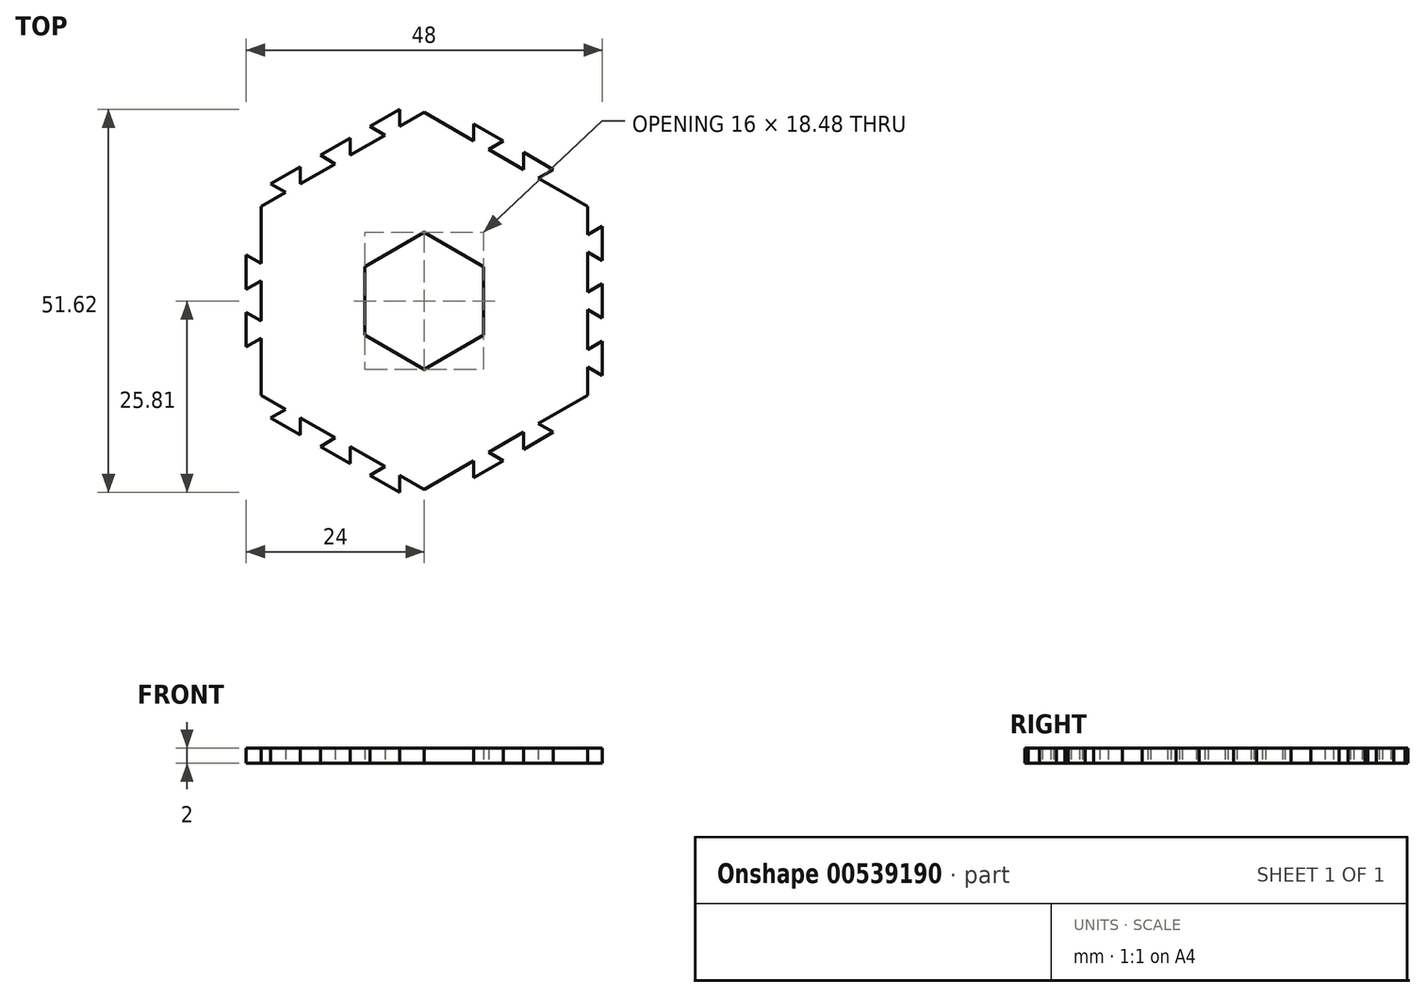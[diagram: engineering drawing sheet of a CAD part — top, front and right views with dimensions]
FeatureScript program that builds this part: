
annotation { "Feature Type Name" : "Feature", "Feature Type Description" : "" }
export const myFeature = defineFeature(function(context is Context, id is Id, definition is map)
    precondition{}
    {
        {
            assignVariable(context, id + "F0", {"name" : "thick", "anyValue" : 2});
        }
        {
            assignVariable(context, id + "F1", {"name" : "depth", "anyValue" : 0});
        }
        {
            var Q0;
            Q0=qCreatedBy(makeId("Top.planeOp"),FACE);
            var sketch = newSketch(context, id + "F2", { "sketchPlane" : qUnion([Q0])});
            skCircle(sketch, "E0.cCircle", {"center": v(0, 0) * mm, "radius": 20 * mm, "construction": true});
            skLineSegment(sketch, "E0.0", {"start": v(-20, -11.55) * mm, "end": v(-20, 11.55) * mm, "construction": true});
            skLineSegment(sketch, "E0.1", {"start": v(-20, 11.55) * mm, "end": v(0, 23.1) * mm, "construction": true});
            skLineSegment(sketch, "E0.2", {"start": v(0, 23.1) * mm, "end": v(20, 11.55) * mm, "construction": true});
            skLineSegment(sketch, "E0.3", {"start": v(20, 11.55) * mm, "end": v(20, -11.55) * mm, "construction": true});
            skLineSegment(sketch, "E0.4", {"start": v(20, -11.55) * mm, "end": v(0, -23.1) * mm, "construction": true});
            skLineSegment(sketch, "E0.5", {"start": v(0, -23.1) * mm, "end": v(-20, -11.55) * mm, "construction": true});
            skPoint(sketch, "E0.0.midPoint", {"position": v(-20, 0) * mm});
            skSolve(sketch);
        }
        {
            var Q0;
            Q0=qCreatedBy(makeId("Top.planeOp"),FACE);
            var sketch = newSketch(context, id + "F3", { "sketchPlane" : qUnion([Q0])});
            skPoint(sketch, "E1.1", {"position": v(-20, 11.55) * mm});
            skPoint(sketch, "E1.3", {"position": v(-20, -11.55) * mm});
            skPoint(sketch, "E1.4", {"position": v(-18, 0) * mm});
            skPoint(sketch, "E1.5", {"position": v(-20, 0) * mm});
            skPoint(sketch, "E1.6", {"position": v(0, 0) * mm});
            skCircle(sketch, "E2.cCircle", {"center": v(-18, 0) * mm, "radius": 8 * mm, "construction": true});
            skLineSegment(sketch, "E2.0", {"start": v(-26, -4.62) * mm, "end": v(-26, 4.62) * mm, "construction": true});
            skLineSegment(sketch, "E2.1", {"start": v(-26, 4.62) * mm, "end": v(-18, 9.24) * mm, "construction": true});
            skLineSegment(sketch, "E2.2", {"start": v(-18, 9.24) * mm, "end": v(-10, 4.62) * mm});
            skLineSegment(sketch, "E2.3", {"start": v(-10, 4.62) * mm, "end": v(-10, -4.62) * mm});
            skLineSegment(sketch, "E2.4", {"start": v(-10, -4.62) * mm, "end": v(-18, -9.24) * mm});
            skLineSegment(sketch, "E2.5", {"start": v(-18, -9.24) * mm, "end": v(-26, -4.62) * mm, "construction": true});
            skPoint(sketch, "E2.0.midPoint", {"position": v(-26, 0) * mm});
            skLineSegment(sketch, "E3", {"start": v(-18, 9.24) * mm, "end": v(-18, -9.24) * mm});
            skLineSegment(sketch, "E4", {"start": v(-20, 11.55) * mm, "end": v(-20, -11.55) * mm});
            skLineSegment(sketch, "E5", {"start": v(-8, 4.62) * mm, "end": v(-8, -4.62) * mm});
            skLineSegment(sketch, "E6", {"start": v(-8, -4.62) * mm, "end": v(-20, -11.55) * mm});
            skLineSegment(sketch, "E7", {"start": v(-8, 4.62) * mm, "end": v(-20, 11.55) * mm});
            skLineSegment(sketch, "E8", {"start": v(-20, -11.55) * mm, "end": v(-22, -12.7) * mm});
            skLineSegment(sketch, "E9", {"start": v(-22, -12.7) * mm, "end": v(-22, 12.7) * mm});
            skLineSegment(sketch, "E10", {"start": v(-22, 12.7) * mm, "end": v(-20, 11.55) * mm});
            skSolve(sketch);
        }
        {
            var Q0;
            Q0=makeQuery(id+"F3.imprint","IMPRINT",FACE,{"disambiguationData":[TD([[makeQuery(id+"F3.imprint","IMPRINT",EDGE,{"derivedFrom":sQuery(id+"F3.wireOp",EDGE,"E2.2")}),1.0]])]});
            var Q1;
            Q1=makeQuery(id+"F3.imprint","IMPRINT",FACE,{"disambiguationData":[TD([[makeQuery(id+"F3.imprint","IMPRINT",EDGE,{"derivedFrom":sQuery(id+"F3.wireOp",EDGE,"E2.2")}),-1.0]])]});
            extrude(context, id + "F4", {"entities" : qUnion([Q0, Q1]), "depth" : (getVariable(context, 'thick')) * mm, "offsetDistance" : 25 * mm});
        }
        {
            var Q0;
            Q0=makeQuery(id+"F3.imprint","IMPRINT",FACE,{"disambiguationData":[TD([[makeQuery(id+"F3.imprint","IMPRINT",EDGE,{"derivedFrom":sQuery(id+"F3.wireOp",EDGE,"E4")}),-1.0]])]});
            extrude(context, id + "F5", {"entities" : qUnion([Q0]), "operationType" : NewBodyOperationType.ADD, "depth" : (getVariable(context, 'depth') + getVariable(context, 'thick')) * mm, "offsetDistance" : 25 * mm});
        }
        {
            var Q0;
            Q0=makeQuery(id+"F4.opExtrude","SWEPT_BODY",BODY,{"disambiguationData":[OSD([sQuery(id+"F3.wireOp",EDGE,"E2.2"),sQuery(id+"F3.wireOp",EDGE,"E2.3"),sQuery(id+"F3.wireOp",EDGE,"E2.4"),sQuery(id+"F3.wireOp",EDGE,"E3"),sQuery(id+"F3.wireOp",EDGE,"E4"),sQuery(id+"F3.wireOp",EDGE,"E5"),sQuery(id+"F3.wireOp",EDGE,"E6"),sQuery(id+"F3.wireOp",EDGE,"E7")])]});
            var Q1;
            Q1=sQuery(id+"F2.wireOp",EDGE,"E0.cCircle");
            circularPattern(context, id + "F6", {"operationType" : NewBodyOperationType.ADD, "entities" : qUnion([Q0]), "axis" : qUnion([Q1]), "angle" : 60 * degree, "instanceCount" : 2, "equalSpace" : true});
        }
        {
            var Q0;
            Q0=qCreatedBy(makeId("Top.planeOp"),FACE);
            var sketch = newSketch(context, id + "F7", { "sketchPlane" : qUnion([Q0])});
            skLineSegment(sketch, "E11.0", {"start": v(-22, -12.7) * mm, "end": v(-22, 12.7) * mm});
            skLineSegment(sketch, "E12", {"start": v(-22, -2.71) * mm, "end": v(-24, -1.56) * mm});
            skLineSegment(sketch, "E13", {"start": v(-24, -6.18) * mm, "end": v(-22, -5.02) * mm});
            skLineSegment(sketch, "E14", {"start": v(-24, -1.56) * mm, "end": v(-24, -2.71) * mm});
            skLineSegment(sketch, "E15", {"start": v(-24, -2.71) * mm, "end": v(-24, -5.02) * mm});
            skLineSegment(sketch, "E16", {"start": v(-24, -5.02) * mm, "end": v(-24, -6.18) * mm});
            skLineSegment(sketch, "E17", {"start": v(-22, -2.71) * mm, "end": v(-22, -5.02) * mm});
            skLineSegment(sketch, "E18", {"start": v(-22, -5.43) * mm, "end": v(-24, -6.58) * mm});
            skLineSegment(sketch, "E19", {"start": v(-24, -6.58) * mm, "end": v(-24, -8.9) * mm});
            skLineSegment(sketch, "E20", {"start": v(-24, -8.9) * mm, "end": v(-22, -10.05) * mm});
            skLineSegment(sketch, "E21", {"start": v(-22, -10.05) * mm, "end": v(-22, -5.43) * mm});
            skLineSegment(sketch, "E22.0.1.0", {"start": v(-22, 5.02) * mm, "end": v(-24, 6.18) * mm});
            skLineSegment(sketch, "E22.0.1.1", {"start": v(-22, -2.3) * mm, "end": v(-22, 2.3) * mm});
            skLineSegment(sketch, "E22.0.1.2", {"start": v(-22, 5.02) * mm, "end": v(-22, 2.71) * mm});
            skLineSegment(sketch, "E22.0.1.3", {"start": v(-24, 2.71) * mm, "end": v(-24, 1.56) * mm});
            skLineSegment(sketch, "E22.0.1.4", {"start": v(-24, -1.15) * mm, "end": v(-22, -2.3) * mm});
            skLineSegment(sketch, "E22.0.1.5", {"start": v(-24, 1.15) * mm, "end": v(-24, -1.15) * mm});
            skLineSegment(sketch, "E22.0.1.6", {"start": v(-24, 6.18) * mm, "end": v(-24, 5.02) * mm});
            skLineSegment(sketch, "E22.0.1.7", {"start": v(-24, 5.02) * mm, "end": v(-24, 2.71) * mm});
            skLineSegment(sketch, "E22.0.1.8", {"start": v(-24, 1.56) * mm, "end": v(-22, 2.71) * mm});
            skLineSegment(sketch, "E22.0.1.9", {"start": v(-22, 2.3) * mm, "end": v(-24, 1.15) * mm});
            skLineSegment(sketch, "E22.0.2.1", {"start": v(-22, 5.43) * mm, "end": v(-22, 10.05) * mm});
            skLineSegment(sketch, "E22.0.2.4", {"start": v(-24, 6.58) * mm, "end": v(-22, 5.43) * mm});
            skLineSegment(sketch, "E22.0.2.5", {"start": v(-24, 8.9) * mm, "end": v(-24, 6.58) * mm});
            skLineSegment(sketch, "E22.0.2.9", {"start": v(-22, 10.05) * mm, "end": v(-24, 8.9) * mm});
            skLineSegment(sketch, "E22.direction1", {"start": v(-28.4, -1.56) * mm, "end": v(-24, -1.56) * mm, "construction": true});
            skLineSegment(sketch, "E22.direction2", {"start": v(-24, -1.56) * mm, "end": v(-24, 6.18) * mm, "construction": true});
            skPoint(sketch, "E23", {"position": v(-22, 0) * mm});
            skPoint(sketch, "E24.center", {"position": v(0, 0) * mm});
            skLineSegment(sketch, "E25.1.0", {"start": v(-7.65, -23.3) * mm, "end": v(-5.65, -22.14) * mm});
            skLineSegment(sketch, "E25.1.1", {"start": v(-9.65, -19.83) * mm, "end": v(-9.65, -22.14) * mm});
            skLineSegment(sketch, "E25.1.2", {"start": v(-9.65, -22.14) * mm, "end": v(-7.65, -23.3) * mm});
            skLineSegment(sketch, "E25.1.3", {"start": v(-5.65, -22.14) * mm, "end": v(-9.65, -19.83) * mm});
            skLineSegment(sketch, "E25.1.4", {"start": v(-6.3, -24.08) * mm, "end": v(-4.3, -25.23) * mm});
            skLineSegment(sketch, "E25.1.5", {"start": v(-7.3, -23.5) * mm, "end": v(-6.3, -24.08) * mm});
            skLineSegment(sketch, "E25.1.6", {"start": v(-4.3, -25.23) * mm, "end": v(-3.3, -25.8) * mm});
            skLineSegment(sketch, "E25.1.7", {"start": v(-3.3, -25.8) * mm, "end": v(-3.3, -23.5) * mm});
            skLineSegment(sketch, "E25.1.8", {"start": v(-5.3, -22.34) * mm, "end": v(-7.3, -23.5) * mm});
            skLineSegment(sketch, "E25.1.9", {"start": v(-5.3, -22.34) * mm, "end": v(-3.3, -23.5) * mm});
            skPoint(sketch, "E25.center", {"position": v(3.35, 1.93) * mm});
            skLineSegment(sketch, "E26.1.0.0", {"start": v(-16.35, -15.96) * mm, "end": v(-16.35, -18.27) * mm});
            skLineSegment(sketch, "E26.1.0.1", {"start": v(-11, -21.36) * mm, "end": v(-10, -21.94) * mm});
            skLineSegment(sketch, "E26.1.0.2", {"start": v(-12, -18.48) * mm, "end": v(-14, -19.63) * mm});
            skLineSegment(sketch, "E26.1.0.3", {"start": v(-14, -19.63) * mm, "end": v(-13, -20.2) * mm});
            skLineSegment(sketch, "E26.1.0.4", {"start": v(-13, -20.2) * mm, "end": v(-11, -21.36) * mm});
            skLineSegment(sketch, "E26.1.0.5", {"start": v(-12.35, -18.27) * mm, "end": v(-16.35, -15.96) * mm});
            skLineSegment(sketch, "E26.1.0.6", {"start": v(-14.35, -19.43) * mm, "end": v(-12.35, -18.27) * mm});
            skLineSegment(sketch, "E26.1.0.7", {"start": v(-12, -18.48) * mm, "end": v(-10, -19.63) * mm});
            skLineSegment(sketch, "E26.1.0.8", {"start": v(-10, -21.94) * mm, "end": v(-10, -19.63) * mm});
            skLineSegment(sketch, "E26.1.0.9", {"start": v(-16.35, -18.27) * mm, "end": v(-14.35, -19.43) * mm});
            skLineSegment(sketch, "E26.direction1", {"start": v(-9.65, -22.14) * mm, "end": v(-16.35, -18.27) * mm, "construction": true});
            skLineSegment(sketch, "E27.3.2.0", {"start": v(-17.7, -17.5) * mm, "end": v(-16.7, -18.07) * mm});
            skLineSegment(sketch, "E27.6.2.0", {"start": v(-18.7, -14.6) * mm, "end": v(-20.7, -15.76) * mm});
            skLineSegment(sketch, "E27.9.2.0", {"start": v(-20.7, -15.76) * mm, "end": v(-19.7, -16.34) * mm});
            skLineSegment(sketch, "E27.12.2.0", {"start": v(-19.7, -16.34) * mm, "end": v(-17.7, -17.5) * mm});
            skLineSegment(sketch, "E27.21.2.0", {"start": v(-18.7, -14.6) * mm, "end": v(-16.7, -15.76) * mm});
            skLineSegment(sketch, "E27.24.2.0", {"start": v(-16.7, -18.07) * mm, "end": v(-16.7, -15.76) * mm});
            skPoint(sketch, "E28.positionSnap0", {"position": v(-11, -19.05) * mm});
            skSolve(sketch);
        }
        {
            var Q0;
            Q0=makeQuery(id+"F7.imprint","IMPRINT",FACE,{"disambiguationData":[TD([[makeQuery(id+"F7.imprint","IMPRINT",EDGE,{"derivedFrom":sQuery(id+"F7.wireOp",EDGE,"E22.0.1.0")}),1.0]])]});
            var Q1;
            Q1=makeQuery(id+"F7.imprint","IMPRINT",FACE,{"disambiguationData":[TD([[makeQuery(id+"F7.imprint","IMPRINT",EDGE,{"derivedFrom":sQuery(id+"F7.wireOp",EDGE,"E12")}),1.0]])]});
            var Q2;
            Q2=makeQuery(id+"F7.imprint","IMPRINT",FACE,{"disambiguationData":[TD([[makeQuery(id+"F7.imprint","IMPRINT",EDGE,{"derivedFrom":sQuery(id+"F7.wireOp",EDGE,"E27.3.2.0")}),1.0]])]});
            var Q3;
            Q3=makeQuery(id+"F7.imprint","IMPRINT",FACE,{"disambiguationData":[TD([[makeQuery(id+"F7.imprint","IMPRINT",EDGE,{"derivedFrom":sQuery(id+"F7.wireOp",EDGE,"E26.1.0.1")}),1.0]])]});
            var Q4;
            Q4=makeQuery(id+"F7.imprint","IMPRINT",FACE,{"disambiguationData":[TD([[makeQuery(id+"F7.imprint","IMPRINT",EDGE,{"derivedFrom":sQuery(id+"F7.wireOp",EDGE,"E25.1.4")}),1.0]])]});
            var Q5;
            Q5=makeQuery(id+"F6.opPattern","COPY",FACE,{"derivedFrom":makeQuery(id+"F5.opExtrude","CAP_FACE",FACE,{"disambiguationData":[OSD([sQuery(id+"F3.wireOp",EDGE,"E4"),sQuery(id+"F3.wireOp",EDGE,"E8"),sQuery(id+"F3.wireOp",EDGE,"E9"),sQuery(id+"F3.wireOp",EDGE,"E10")])],"isStart":false}),"instanceName":"1"});
            extrude(context, id + "F8", {"entities" : qUnion([Q0, Q1, Q2, Q3, Q4]), "operationType" : NewBodyOperationType.ADD, "endBound" : BoundingType.UP_TO_SURFACE, "depth" : 25 * mm, "endBoundEntityFace" : qUnion([Q5]), "offsetDistance" : 25 * mm});
        }
        {
            var Q0;
            Q0=makeQuery(id+"F4.opExtrude","SWEPT_BODY",BODY,{"disambiguationData":[OSD([sQuery(id+"F3.wireOp",EDGE,"E2.2"),sQuery(id+"F3.wireOp",EDGE,"E2.3"),sQuery(id+"F3.wireOp",EDGE,"E2.4"),sQuery(id+"F3.wireOp",EDGE,"E3"),sQuery(id+"F3.wireOp",EDGE,"E4"),sQuery(id+"F3.wireOp",EDGE,"E5"),sQuery(id+"F3.wireOp",EDGE,"E6"),sQuery(id+"F3.wireOp",EDGE,"E7")])]});
            var Q1;
            Q1=makeQuery(id+"F6.opPattern","COPY",BODY,{"derivedFrom":makeQuery(id+"F4.opExtrude","SWEPT_BODY",BODY,{"disambiguationData":[OSD([sQuery(id+"F3.wireOp",EDGE,"E2.2"),sQuery(id+"F3.wireOp",EDGE,"E2.3"),sQuery(id+"F3.wireOp",EDGE,"E2.4"),sQuery(id+"F3.wireOp",EDGE,"E3"),sQuery(id+"F3.wireOp",EDGE,"E4"),sQuery(id+"F3.wireOp",EDGE,"E5"),sQuery(id+"F3.wireOp",EDGE,"E6"),sQuery(id+"F3.wireOp",EDGE,"E7")])]}),"instanceName":"1"});
            var Q2;
            Q2=sQuery(id+"F2.wireOp",EDGE,"E0.cCircle");
            circularPattern(context, id + "F9", {"operationType" : NewBodyOperationType.ADD, "entities" : qUnion([Q0, Q1]), "axis" : qUnion([Q2]), "angle" : 240 * degree, "instanceCount" : 3, "equalSpace" : true});
        }
    });
